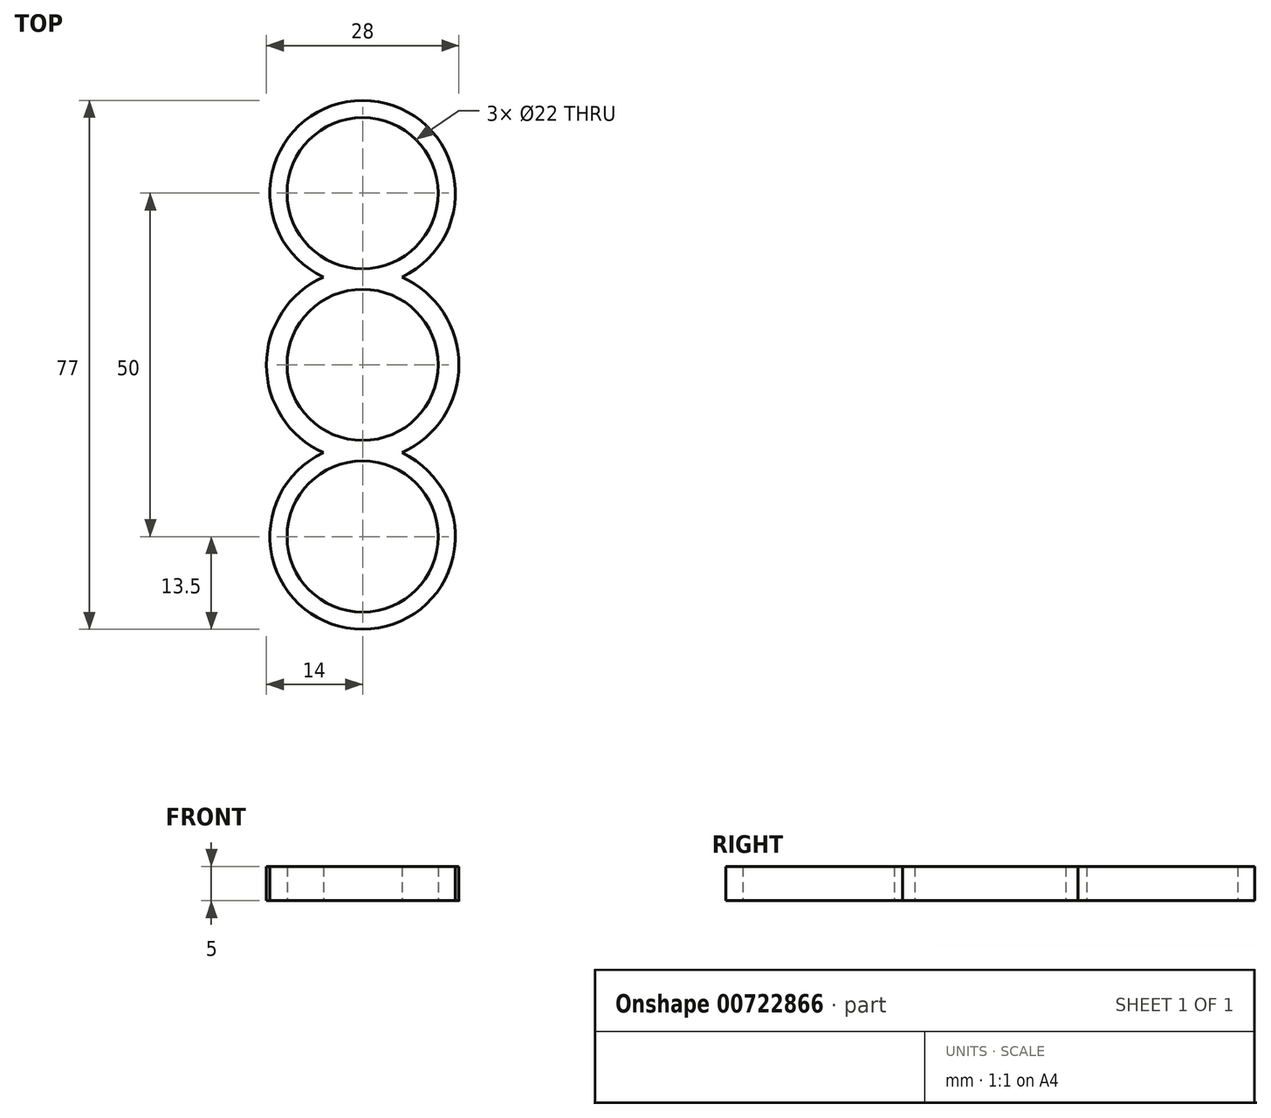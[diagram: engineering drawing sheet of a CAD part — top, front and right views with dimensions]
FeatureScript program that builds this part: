
annotation { "Feature Type Name" : "Feature", "Feature Type Description" : "" }
export const myFeature = defineFeature(function(context is Context, id is Id, definition is map)
    precondition{}
    {
        {
            var Q0;
            Q0=qCreatedBy(makeId("Top.planeOp"),FACE);
            var sketch = newSketch(context, id + "F0", { "sketchPlane" : qUnion([Q0])});
            skCircle(sketch, "E0", {"center": v(0, 0) * mm, "radius": 11 * mm});
            skLineSegment(sketch, "E1", {"start": v(0, 11) * mm, "end": v(0, 14) * mm});
            skCircle(sketch, "E2", {"center": v(0, 25) * mm, "radius": 11 * mm});
            skArc(sketch, "E3", {"start": v(5.73, 12.78) * mm, "mid": v(0, 38.5) * mm, "end": v(-5.73, 12.78) * mm});
            skArc(sketch, "E4", {"start": v(-5.73, 12.78) * mm, "mid": v(-14, 0) * mm, "end": v(-5.73, -12.78) * mm});
            skLineSegment(sketch, "E5", {"start": v(0, 0) * mm, "end": v(0, -14) * mm});
            skCircle(sketch, "E6", {"center": v(0, -25) * mm, "radius": 11 * mm});
            skArc(sketch, "E7", {"start": v(-5.73, -12.78) * mm, "mid": v(0, -38.5) * mm, "end": v(5.73, -12.78) * mm});
            skArc(sketch, "E8.trimOffspring", {"start": v(5.73, -12.78) * mm, "mid": v(14, 0) * mm, "end": v(5.73, 12.77) * mm});
            skSolve(sketch);
        }
        {
            var Q0;
            Q0=makeQuery(id+"F0.imprint","IMPRINT",FACE,{"disambiguationData":[TD([[makeQuery(id+"F0.imprint","IMPRINT",EDGE,{"derivedFrom":sQuery(id+"F0.wireOp",EDGE,"E2")}),-1.0]])]});
            extrude(context, id + "F1", {"entities" : qUnion([Q0]), "depth" : 5 * mm, "offsetDistance" : 25 * mm});
        }
    });
